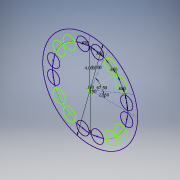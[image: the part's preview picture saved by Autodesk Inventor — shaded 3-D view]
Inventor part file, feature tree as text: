
AUTODESK INVENTOR PART (.ipt)
format: ipt  version: 2016 (Build 200138000, 138)  size: 106,496 bytes
history: native  units: in
note: dims shown in document units (in); Inventor stores cm internally (conversion verified against a paired STEP export)
features: sketch x1
ambient origin geometry x8: Origin, YZ Plane, XZ Plane, XY Plane, X Axis, Y Axis, Z Axis, Center Point
feature tree (1):
  sketch  "Sketch1"  dims[d8=0.19in d9=0.19in d15=5.0in d16=22.5deg d17=67.5deg d18=4.0in d19=0.65in d20=0.65in d21=0.65in d22=0.65in]
